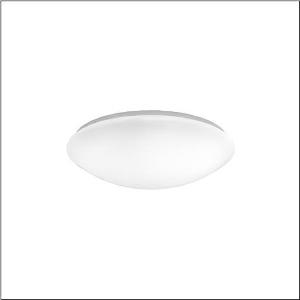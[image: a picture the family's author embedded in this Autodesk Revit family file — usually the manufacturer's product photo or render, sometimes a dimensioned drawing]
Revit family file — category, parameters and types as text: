
# Revit family: round_31_b_5pja112001a
name_source: partatom
category: Lighting Fixtures
units: mm (PartAtom-declared; Revit-internal decimal feet)

## family parameters
Cut with Voids When Loaded = No
Host = Face
Light Source = No
Part Type = Normal
Room Calculation Point = No
Round Connector Dimension = Use Diameter
Shared = No

## types (1)
- Round 31 B (1 x LED, 2300 lm, 19 W, 3000K)
    Apparent Load = 19 VA
    CIE Flux Codes = 42 71 89 88 100
    Color Rendering = 80
    Color Temperature = 3000K
    Default Elevation = 1800 mm
    Description = Round 31 B, wall and ceiling luminaire, primary optical cover: enclosure, of PMMA, light emission: direct distribution, primary light characteristic: symmetric, installation type: surface-mounted, LED, rated luminous flux: 2.300lm, luminous efficacy: 121lm/W, light colour: 830, colour temperature: 3000K, with terminal, 3+2-pole, max. 2.5mm², mains connection: 230V, AC, 50/60Hz, rated input power: 19W, luminaire housing, round, of steel, white, diameter: 360mm, height: 95mm, protection rating (complete): IP40, insulation class (complete): insulation class I (protective earthing), certification: CE, impact resistance: IK02, permissible operating ambient temperature: -20..+25°C, packaging unit: 1 piece
    Height = 95 mm
    Lamp = 1 x LED
    Lamp Light Flux = 2300 lm
    Lamp Power = 19 W
    Lamp count = 1
    Length = 360 mm
    Luminous efficacy = 121 lm/W
    Manufacturer = Siteco
    ModVariant = No
    Model = 5PJA112001A
    Mounting Place = Ceiling
    Mounting Type = Surface mounted
    Number of Poles = 1
    OnlyDefault = Yes
    Power Factor = 1
    Product Name = Round 31 B
    Product group = wall and ceiling luminaire
    ProductGroupID = 302
    Protection Class = Protection class I
    Protection Degree = IP 40
    RLX_Detail_Level = 1
    RLX_Emergency_Light_Flux = 0 lm
    RLX_Emergency_Type = 0
    RLX_Emergency_Type_DB = No
    RlxData = <blob elided: 10985 chars, md5=0eed61e9>
    Socket = socket
    Standby Power = 0 W
    System Light Flux = 2300 lm
    System Power = 19 W
    Type Comments = Product without accessories
    Type Image = l_1258315.jpg
    URL = http://relux.com
    VarID = ---
    Voltage = 0 V
    Weight = 0.00 kg
    Width = 0 mm  [stored 0 ft]

note: [stored X ft] marks values corroborated as IEEE doubles in the binary element streams (Revit-internal decimal feet)

## geometry (parser evidence)
native form markers: Sweep x13
no freeform markers — native parametric forms only
